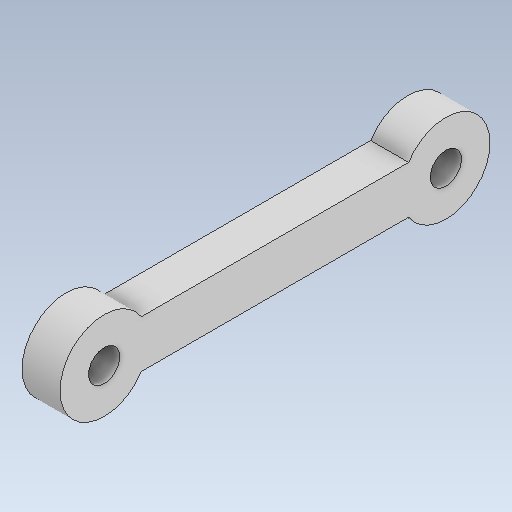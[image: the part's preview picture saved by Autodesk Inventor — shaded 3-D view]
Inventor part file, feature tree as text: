
AUTODESK INVENTOR PART (.ipt)
format: ipt  version: 2020 (Build 240168000, 168)  size: 116,224 bytes
history: native  units: in
note: dims shown in document units (in); Inventor stores cm internally (conversion verified against a paired STEP export)
features: extrude x1, sketch x1
ambient origin geometry x8: Origin, YZ Plane, XZ Plane, XY Plane, X Axis, Y Axis, Z Axis, Center Point
bodies: Solid1 (feature_tree)
feature tree (2):
  extrude  "Extrusion1"  Depth=1.4173in
  sketch  "Sketch1"  dims[d0=0.1299in d1=1.4173in d2=0.1181in d3=0.1181in d4=0.1969in d5=0.1575in d6=0.0in]
